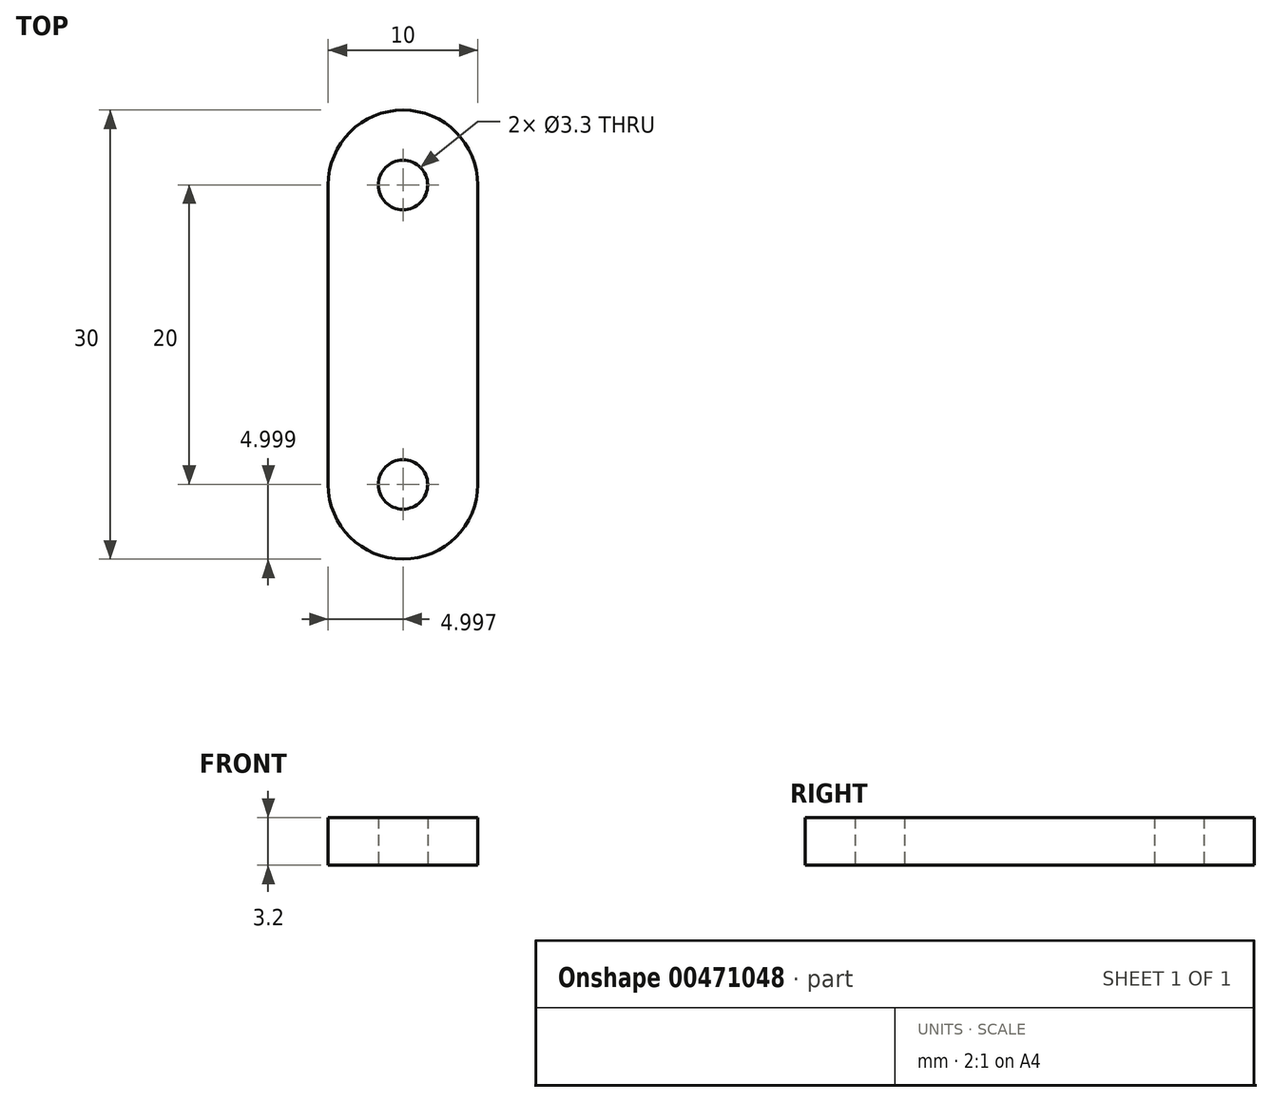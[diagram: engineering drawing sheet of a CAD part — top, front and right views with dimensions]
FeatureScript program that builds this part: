
annotation { "Feature Type Name" : "Feature", "Feature Type Description" : "" }
export const myFeature = defineFeature(function(context is Context, id is Id, definition is map)
    precondition{}
    {
        {
            var Q0;
            Q0=qCreatedBy(makeId("Top.planeOp"),FACE);
            var sketch = newSketch(context, id + "F0", { "sketchPlane" : qUnion([Q0])});
            skLineSegment(sketch, "E0", {"start": v(-29.16, 18.88) * mm, "end": v(-29.16, -1.12) * mm});
            skLineSegment(sketch, "E1", {"start": v(-19.16, 18.88) * mm, "end": v(-19.16, -1.12) * mm});
            skArc(sketch, "E2", {"start": v(-19.16, 18.88) * mm, "mid": v(-24.16, 23.88) * mm, "end": v(-29.16, 18.88) * mm});
            skArc(sketch, "E3", {"start": v(-29.16, -1.12) * mm, "mid": v(-24.16, -6.12) * mm, "end": v(-19.16, -1.12) * mm});
            skCircle(sketch, "E4", {"center": v(-24.16, 18.88) * mm, "radius": 1.65 * mm});
            skCircle(sketch, "E5", {"center": v(-24.16, -1.12) * mm, "radius": 1.65 * mm});
            skSolve(sketch);
        }
        {
            var Q0;
            Q0 = qSketchRegion(id + "F0", true);
            extrude(context, id + "F1", {"entities" : qUnion([Q0]), "depth" : 3.2 * mm, "offsetDistance" : 25 * mm});
        }
    });
